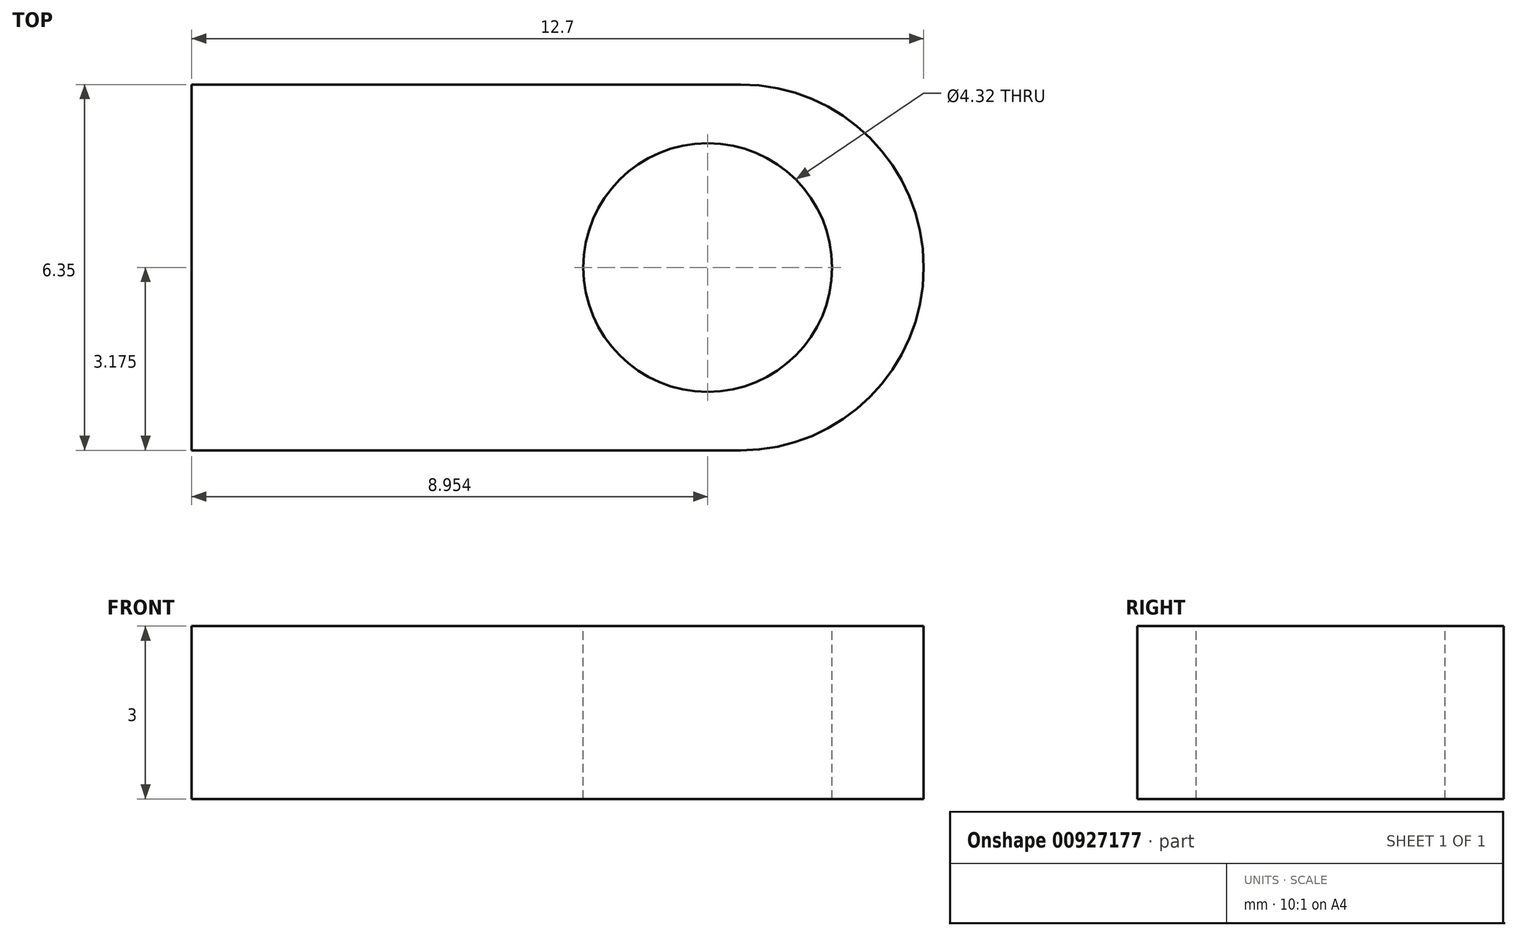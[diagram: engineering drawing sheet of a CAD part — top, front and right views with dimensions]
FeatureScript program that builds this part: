
annotation { "Feature Type Name" : "Feature", "Feature Type Description" : "" }
export const myFeature = defineFeature(function(context is Context, id is Id, definition is map)
    precondition{}
    {
        {
            var Q0;
            Q0=qCreatedBy(makeId("Top.planeOp"),FACE);
            var sketch = newSketch(context, id + "F0", { "sketchPlane" : qUnion([Q0])});
            skLineSegment(sketch, "E0.bottom", {"start": v(0, 0) * mm, "end": v(12.7, 0) * mm});
            skLineSegment(sketch, "E0.top", {"start": v(0, 6.35) * mm, "end": v(12.7, 6.35) * mm});
            skLineSegment(sketch, "E0.left", {"start": v(0, 0) * mm, "end": v(0, 6.35) * mm});
            skLineSegment(sketch, "E0.right", {"start": v(12.7, 0) * mm, "end": v(12.7, 6.35) * mm});
            skSolve(sketch);
        }
        {
            var Q0;
            Q0=makeQuery(id+"F0.imprint","IMPRINT",FACE,{"disambiguationData":[TD([[makeQuery(id+"F0.imprint","IMPRINT",EDGE,{"derivedFrom":sQuery(id+"F0.wireOp",EDGE,"E0.bottom")}),1.0]])]});
            extrude(context, id + "F1", {"entities" : qUnion([Q0]), "depth" : 3 * mm, "offsetDistance" : 25.4 * mm});
        }
        {
            var Q0;
            Q0=makeQuery(id+"F1.opExtrude","CAP_FACE",FACE,{"disambiguationData":[OSD([sQuery(id+"F0.wireOp",EDGE,"E0.bottom"),sQuery(id+"F0.wireOp",EDGE,"E0.top"),sQuery(id+"F0.wireOp",EDGE,"E0.left"),sQuery(id+"F0.wireOp",EDGE,"E0.right")])],"isStart":false});
            var sketch = newSketch(context, id + "F2", { "sketchPlane" : qUnion([Q0])});
            skLineSegment(sketch, "E1", {"start": v(12.7, 3.17) * mm, "end": v(0, 3.17) * mm, "construction": true});
            skCircle(sketch, "E2", {"center": v(8.95, 3.17) * mm, "radius": 2.16 * mm});
            skSolve(sketch);
        }
        {
            var Q0;
            Q0=makeQuery(id+"F1.opExtrude","SWEPT_EDGE",EDGE,{"disambiguationData":[OSD([sQuery(id+"F0.wireOp",EDGE,"E0.top"),sQuery(id+"F0.wireOp",EDGE,"E0.right")])]});
            var Q1;
            Q1=makeQuery(id+"F1.opExtrude","SWEPT_EDGE",EDGE,{"disambiguationData":[OSD([sQuery(id+"F0.wireOp",EDGE,"E0.bottom"),sQuery(id+"F0.wireOp",EDGE,"E0.right")])]});
            fillet(context, id + "F3", {"entities" : qUnion([Q0, Q1]), "radius" : 3.17 * mm, "tangentPropagation" : true, "allowEdgeOverflow" : false});
        }
        {
            var Q0;
            Q0=makeQuery(id+"F2.imprint","IMPRINT",FACE,{"disambiguationData":[TD([[makeQuery(id+"F2.imprint","IMPRINT",EDGE,{"derivedFrom":sQuery(id+"F2.wireOp",EDGE,"E2")}),1.0]])]});
            extrude(context, id + "F4", {"entities" : qUnion([Q0]), "operationType" : NewBodyOperationType.REMOVE, "oppositeDirection" : true, "depth" : 25.4 * mm, "offsetDistance" : 25.4 * mm});
        }
    });
